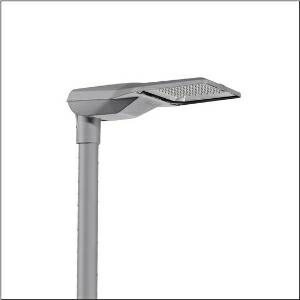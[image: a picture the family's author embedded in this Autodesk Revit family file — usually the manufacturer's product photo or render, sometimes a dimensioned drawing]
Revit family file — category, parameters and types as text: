
# Revit family: streetlight_sl_21_iq_midi___st1_0a_5xe3d41g08nb_8322
name_source: partatom
category: Lighting Fixtures
units: mm (PartAtom-declared; Revit-internal decimal feet)

## family parameters
Cut with Voids When Loaded = No
Host = Face
Light Source = No
Part Type = Normal
Room Calculation Point = No
Round Connector Dimension = Use Diameter
Shared = No

## types (1)
- --- (1 x LED, 24250 lm, 155.5 W, 4000K)
    Apparent Load = 155 VA
    CIE Flux Codes = 40 73 97 100 100
    Color Rendering = 70
    Color Temperature = 4000K
    Default Elevation = 1800 mm
    Description = Streetlight SL 21 iQ midi, mast luminaire, primary light control with lens, of PMMA, primary optical cover: cover, of toughened safety glass, transparent, light distribution: ST1.0a, light emission: direct distribution, primary light characteristic: asymmetric, installation type: post-top, side-entry, LED, High Power LED, rated luminous flux: 24.250lm, luminous efficacy: 156lm/W, light colour: 740, colour temperature: 4000K, control gear: iQ Street-Remote, control: Street-Remote, Auto-Match, Temp-Guard, Lumen-Switch, Night-Set, Smart-Wire, Light-Fading, Desk-Remote (wireless, voltage-free reading and setting of iQ features in the workshop via application-optimized NFC function/RFID function), optimised constant luminous flux control (CLO 2.0), pre-setting: linear dimming characteristic, mains connection: 230..240V, AC, 50/60Hz, start of lifetime: 156W, end of service life: 162W, reduction: 69W, luminaire housing, of diecast aluminium, powder-coated, SITECO metallic grey (DB 702S), corrosivity category C5 high according to DIN EN ISO 12944, please order mast flange separately, inclination adjustable: 0°, 5°, 10°, 15°, sealing non-destructively replaceable, multi-level sealing system, length: 644mm, width: 335mm, height: 110mm, mast flange for spigot size: 42mm (side-entry): 5XC10008XM4, 60/48mm (side-entry/post-top): 5XC10108XM2, 76/60mm (side-entry/post-top): 5XC10108XM1, mounting height: 4..8m, protection rating (complete): IP66, insulation class (complete): insulation class II (safety insulation), certification: CE, ENEC, ENEC+, VDE, impact resistance: IK10, permissible operating ambient temperature for outdoor applications: -40..+50°C, standard-compliant lighting for roads and squares, packaging unit: 1 piece

Light Distribution: ST1.0a
    Height = 111 mm
    Lamp = 1 x LED
    Lamp Light Flux = 24250 lm
    Lamp Power = 155.5 W
    Lamp count = 1
    Length = 644 mm
    Luminous efficacy = 156 lm/W
    Manufacturer = Siteco
    ModVariant = No
    Model = 5XE3D41G08NB
    Number of Poles = 1
    OnlyDefault = Yes
    Power Factor = 1
    Product Name = Streetlight SL 21 iQ midi | ST1.0a
    Product group = mast luminaire | pylon top
    ProductGroupID = 6100
    Protection Class = Protection class II
    Protection Degree = IP 66
    RLX_Detail_Level = 1
    RLX_Emergency_Light_Flux = 0 lm
    RLX_Emergency_Type = 0
    RLX_Emergency_Type_DB = No
    RlxData = <blob elided: 27213 chars, md5=cffd362d>
    Socket = socket
    Standby Power = 0 W
    System Light Flux = 24250 lm
    System Power = 155 W
    Type Comments = factory setting: luminous flux: 100 % | dim-lin: 254 | 823 mA
    Type Image = l_1004298.jpg
    URL = http://relux.com
    VarID = @adj_170247
    Voltage = 0 V
    Weight = 0.00 kg
    Width = 336 mm

## geometry (parser evidence)
native form markers: Blend x4, Sweep x12
no freeform markers — native parametric forms only
